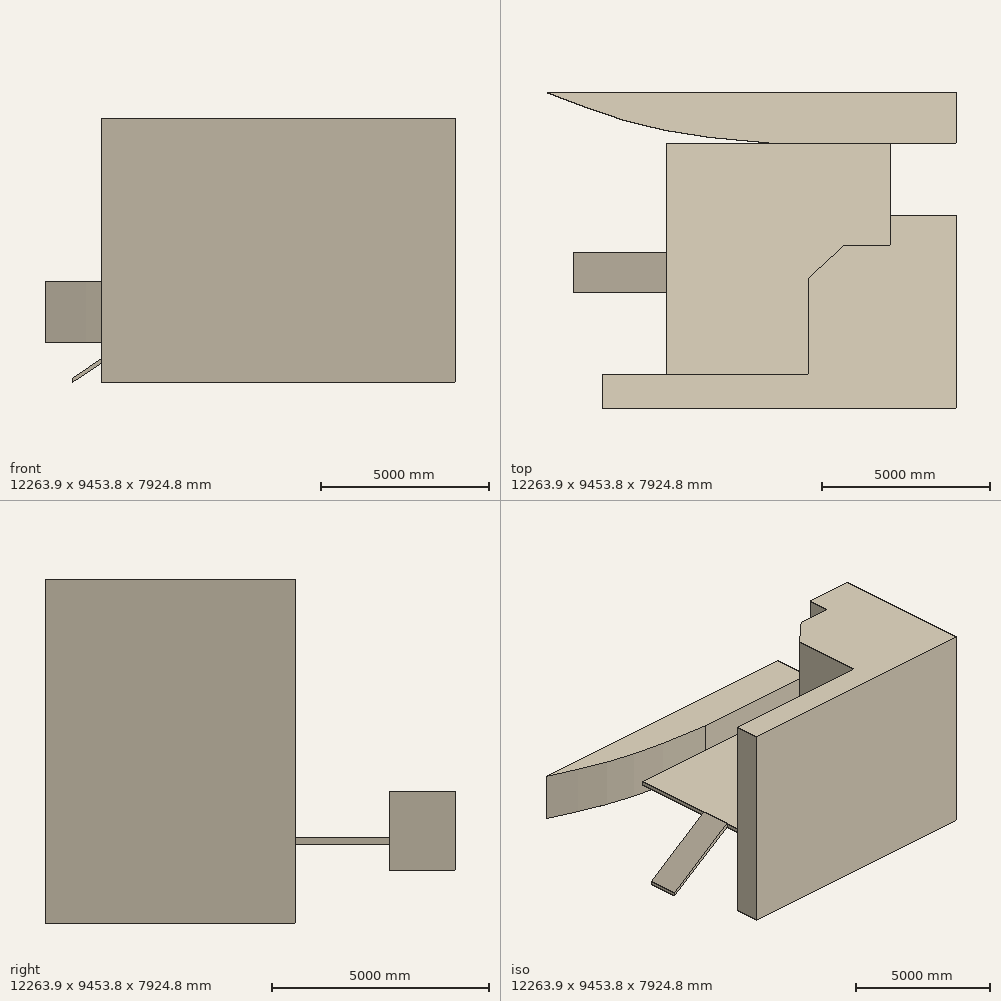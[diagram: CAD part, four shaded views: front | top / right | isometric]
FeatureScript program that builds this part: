
annotation { "Feature Type Name" : "Feature", "Feature Type Description" : "" }
export const myFeature = defineFeature(function(context is Context, id is Id, definition is map)
    precondition{}
    {
        {
            var Q0;
            Q0=qCreatedBy(makeId("Top.planeOp"),FACE);
            var sketch = newSketch(context, id + "F0", { "sketchPlane" : qUnion([Q0])});
            skLineSegment(sketch, "E0", {"start": v(-2166.23, -111.43) * mm, "end": v(2100.97, -111.43) * mm});
            skLineSegment(sketch, "E1", {"start": v(2100.97, -111.43) * mm, "end": v(2100.97, 2769.12) * mm});
            skLineSegment(sketch, "E2", {"start": v(3167.77, 3747.34) * mm, "end": v(4539.37, 3747.34) * mm});
            skLineSegment(sketch, "E3", {"start": v(3167.77, 3747.34) * mm, "end": v(2100.97, 2769.12) * mm});
            skLineSegment(sketch, "E4", {"start": v(4539.37, 3747.34) * mm, "end": v(4539.37, 4645.62) * mm});
            skLineSegment(sketch, "E5", {"start": v(4539.37, 4645.62) * mm, "end": v(6521.51, 4645.62) * mm});
            skLineSegment(sketch, "E6", {"start": v(6521.51, 4645.62) * mm, "end": v(6521.51, -1125.93) * mm});
            skLineSegment(sketch, "E7", {"start": v(6521.51, -1125.93) * mm, "end": v(-4056.05, -1125.93) * mm});
            skLineSegment(sketch, "E8", {"start": v(-4056.05, -1125.93) * mm, "end": v(-4056.05, -111.43) * mm});
            skLineSegment(sketch, "E9", {"start": v(-2166.23, -111.43) * mm, "end": v(-4056.05, -111.43) * mm});
            skLineSegment(sketch, "E10", {"start": v(-2166.23, -111.43) * mm, "end": v(-2166.23, 3747.34) * mm});
            skLineSegment(sketch, "E11", {"start": v(3167.77, 3747.34) * mm, "end": v(-2166.23, 3747.34) * mm});
            skLineSegment(sketch, "E12", {"start": v(6521.51, 6795.34) * mm, "end": v(1130.9, 6795.34) * mm});
            skLineSegment(sketch, "E13", {"start": v(-2166.23, 3747.34) * mm, "end": v(-2166.23, 6795.34) * mm});
            skFitSpline(sketch, "E14", {"points": [v(1130.9, 6795.34) * mm, v(-2775.13, 7318.58) * mm, v(-5742.37, 8327.84) * mm], "startDerivative": vector(-6964.37, 431.83) * mm, "endDerivative": vector(-6944.77, 2618.08) * mm});
            skLineSegment(sketch, "E15", {"start": v(-2166.23, 6795.34) * mm, "end": v(4539.37, 6795.34) * mm});
            skLineSegment(sketch, "E16", {"start": v(-5742.37, 8327.84) * mm, "end": v(6521.51, 8327.84) * mm});
            skLineSegment(sketch, "E17", {"start": v(6521.51, 6795.34) * mm, "end": v(6521.51, 8327.84) * mm});
            skLineSegment(sketch, "E18", {"start": v(4539.37, 6795.34) * mm, "end": v(4539.37, 4645.62) * mm});
            skSolve(sketch);
        }
        {
            var Q0;
            Q0=makeQuery(id+"F0.imprint","IMPRINT",FACE,{"disambiguationData":[TD([[makeQuery(id+"F0.imprint","IMPRINT",EDGE,{"derivedFrom":sQuery(id+"F0.wireOp",EDGE,"E0")}),-1.0]])]});
            extrude(context, id + "F1", {"entities" : qUnion([Q0]), "oppositeDirection" : true, "depth" : 1828.8 * mm, "offsetDistance" : 30.48 * mm, "hasSecondDirection" : true, "secondDirectionOppositeDirection" : false, "secondDirectionDepth" : 6096 * mm});
        }
        {
            var Q0;
            Q0=makeQuery(id+"F0.imprint","IMPRINT",FACE,{"disambiguationData":[TD([[makeQuery(id+"F0.imprint","IMPRINT",EDGE,{"derivedFrom":sQuery(id+"F0.wireOp",EDGE,"E0")}),1.0]])]});
            extrude(context, id + "F2", {"entities" : qUnion([Q0]), "operationType" : NewBodyOperationType.ADD, "depth" : 152.4 * mm, "offsetDistance" : 30.48 * mm});
        }
        {
            var Q0;
            Q0=qCreatedBy(makeId("Front.planeOp"),FACE);
            cPlane(context, id + "F3", {"entities" : qUnion([Q0]), "cplaneType" : CPlaneType.OFFSET, "offset" : 2334.77 * mm, "oppositeDirection" : true, "width" : 152.4 * mm, "height" : 152.4 * mm});
        }
        {
            var Q0;
            Q0=qCreatedBy(id+"F3.planeOp",FACE);
            var sketch = newSketch(context, id + "F4", { "sketchPlane" : qUnion([Q0])});
            skLineSegment(sketch, "E19", {"start": v(-2158.66, 177.23) * mm, "end": v(-4946.1, -1701.72) * mm});
            skLineSegment(sketch, "E20", {"start": v(-4946.1, -1701.72) * mm, "end": v(-4946.1, -1825.6) * mm});
            skLineSegment(sketch, "E21", {"start": v(-4946.1, -1825.6) * mm, "end": v(-2158.66, 0) * mm});
            skLineSegment(sketch, "E22", {"start": v(-2158.66, 0) * mm, "end": v(-2158.66, 177.23) * mm});
            skSolve(sketch);
        }
        {
            var Q0;
            Q0=makeQuery(id+"F4.imprint","IMPRINT",FACE,{"disambiguationData":[TD([[makeQuery(id+"F4.imprint","IMPRINT",EDGE,{"derivedFrom":sQuery(id+"F4.wireOp",EDGE,"E19")}),1.0]])]});
            var Q1;
            Q1=sQuery(id+"F4.wireOp",EDGE,"E20");
            var Q2;
            Q2=sQuery(id+"F4.wireOp",EDGE,"E21");
            var Q3;
            Q3=sQuery(id+"F4.wireOp",EDGE,"E22");
            var Q4;
            Q4=sQuery(id+"F4.wireOp",EDGE,"E19");
            extrude(context, id + "F5", {"entities" : qUnion([Q0]), "operationType" : NewBodyOperationType.ADD, "surfaceEntities" : qUnion([Q1, Q2, Q3, Q4]), "oppositeDirection" : true, "depth" : 1219.2 * mm, "offsetDistance" : 30.48 * mm});
        }
        {
            var Q0;
            Q0=makeQuery(id+"F0.imprint","IMPRINT",FACE,{"disambiguationData":[TD([[makeQuery(id+"F0.imprint","IMPRINT",EDGE,{"derivedFrom":sQuery(id+"F0.wireOp",EDGE,"E2")}),1.0]])]});
            extrude(context, id + "F6", {"entities" : qUnion([Q0]), "operationType" : NewBodyOperationType.ADD, "depth" : 152.4 * mm, "offsetDistance" : 30.48 * mm});
        }
        {
            var Q0;
            Q0=makeQuery(id+"F1.opExtrude","SWEPT_BODY",BODY,{"disambiguationData":[OSD([sQuery(id+"F0.wireOp",EDGE,"E0"),sQuery(id+"F0.wireOp",EDGE,"E1"),sQuery(id+"F0.wireOp",EDGE,"E2"),sQuery(id+"F0.wireOp",EDGE,"E3"),sQuery(id+"F0.wireOp",EDGE,"E4"),sQuery(id+"F0.wireOp",EDGE,"E5"),sQuery(id+"F0.wireOp",EDGE,"E6"),sQuery(id+"F0.wireOp",EDGE,"E7"),sQuery(id+"F0.wireOp",EDGE,"E8"),sQuery(id+"F0.wireOp",EDGE,"E9")])]});
            transform(context, id + "F7", {"entities" : qUnion([Q0]), "transformType" : TransformType.TRANSLATION_3D, "dx" : 0 * mm, "dy" : 0 * mm, "dz" : 0 * mm, "makeCopy" : true});
        }
        {
            var Q0;
            Q0=makeQuery(id+"F7.opPattern","COPY",BODY,{"derivedFrom":makeQuery(id+"F1.opExtrude","SWEPT_BODY",BODY,{"disambiguationData":[OSD([sQuery(id+"F0.wireOp",EDGE,"E0"),sQuery(id+"F0.wireOp",EDGE,"E1"),sQuery(id+"F0.wireOp",EDGE,"E2"),sQuery(id+"F0.wireOp",EDGE,"E3"),sQuery(id+"F0.wireOp",EDGE,"E4"),sQuery(id+"F0.wireOp",EDGE,"E5"),sQuery(id+"F0.wireOp",EDGE,"E6"),sQuery(id+"F0.wireOp",EDGE,"E7"),sQuery(id+"F0.wireOp",EDGE,"E8"),sQuery(id+"F0.wireOp",EDGE,"E9")])]}),"instanceName":"1"});
            deleteBodies(context, id + "F8", {"entities" : qUnion([Q0])});
        }
        {
            var Q0;
            {var subQ1=sQuery(id+"F0.wireOp",EDGE,"E12");Q0=makeQuery(id+"F0.imprint","IMPRINT",FACE,{"disambiguationData":[TD([[makeQuery(id+"F0.imprint","IMPRINT",EDGE,{"derivedFrom":subQ1}),-1.0]])]});}
            extrude(context, id + "F9", {"entities" : qUnion([Q0]), "operationType" : NewBodyOperationType.ADD, "depth" : 1219.2 * mm, "offsetDistance" : 30.48 * mm, "hasSecondDirection" : true, "secondDirectionOppositeDirection" : true, "secondDirectionDepth" : 609.6 * mm});
        }
    });
